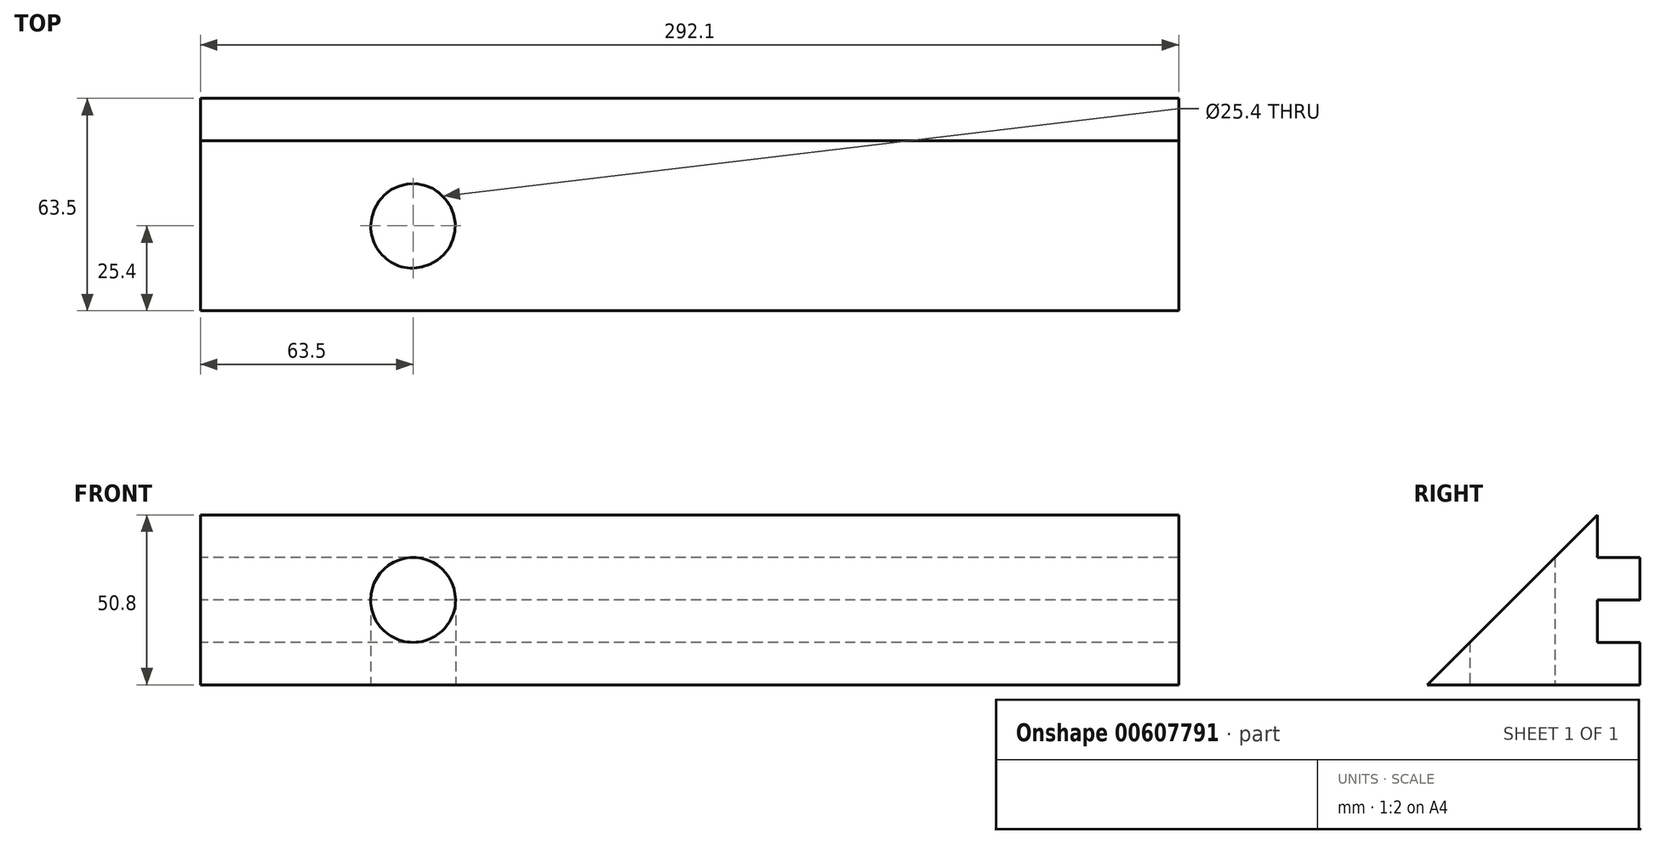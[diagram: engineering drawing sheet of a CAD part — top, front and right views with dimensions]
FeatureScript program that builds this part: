
annotation { "Feature Type Name" : "Feature", "Feature Type Description" : "" }
export const myFeature = defineFeature(function(context is Context, id is Id, definition is map)
    precondition{}
    {
        {
            var Q0;
            Q0=qCreatedBy(makeId("Top.planeOp"),FACE);
            var sketch = newSketch(context, id + "F0", { "sketchPlane" : qUnion([Q0])});
            skLineSegment(sketch, "E0.bottom", {"start": v(0, 0) * mm, "end": v(292.1, 0) * mm});
            skLineSegment(sketch, "E0.top", {"start": v(0, 50.8) * mm, "end": v(292.1, 50.8) * mm});
            skLineSegment(sketch, "E0.left", {"start": v(0, 0) * mm, "end": v(0, 50.8) * mm});
            skLineSegment(sketch, "E0.right", {"start": v(292.1, 0) * mm, "end": v(292.1, 50.8) * mm});
            skLineSegment(sketch, "E1.bottom", {"start": v(0, 0) * mm, "end": v(50.8, 0) * mm});
            skLineSegment(sketch, "E1.top", {"start": v(0, -228.6) * mm, "end": v(50.8, -228.6) * mm});
            skLineSegment(sketch, "E1.left", {"start": v(0, 0) * mm, "end": v(0, -228.6) * mm});
            skLineSegment(sketch, "E1.right", {"start": v(50.8, 0) * mm, "end": v(50.8, -228.6) * mm});
            skLineSegment(sketch, "E2.bottom", {"start": v(292.1, 0) * mm, "end": v(241.3, 0) * mm});
            skLineSegment(sketch, "E2.top", {"start": v(292.1, -228.6) * mm, "end": v(241.3, -228.6) * mm});
            skLineSegment(sketch, "E2.left", {"start": v(292.1, 0) * mm, "end": v(292.1, -228.6) * mm});
            skLineSegment(sketch, "E2.right", {"start": v(241.3, 0) * mm, "end": v(241.3, -228.6) * mm});
            skSolve(sketch);
        }
        {
            var Q0;
            Q0=makeQuery(id+"F0.imprint","IMPRINT",FACE,{"disambiguationData":[TD([[makeQuery(id+"F0.imprint","IMPRINT",EDGE,{"derivedFrom":sQuery(id+"F0.wireOp",EDGE,"E1.bottom")}),-1.0]])]});
            var Q1;
            Q1=makeQuery(id+"F0.imprint","IMPRINT",FACE,{"disambiguationData":[TD([[makeQuery(id+"F0.imprint","IMPRINT",EDGE,{"derivedFrom":sQuery(id+"F0.wireOp",EDGE,"E0.bottom")}),1.0]])]});
            var Q2;
            Q2=makeQuery(id+"F0.imprint","IMPRINT",FACE,{"disambiguationData":[TD([[makeQuery(id+"F0.imprint","IMPRINT",EDGE,{"derivedFrom":sQuery(id+"F0.wireOp",EDGE,"E2.bottom")}),1.0]])]});
            extrude(context, id + "F1", {"entities" : qUnion([Q0, Q1, Q2]), "depth" : 50.8 * mm, "offsetDistance" : 25.4 * mm});
        }
        {
            var Q0;
            Q0=makeQuery(id+"F1.opExtrude","CAP_EDGE",EDGE,{"disambiguationData":[OSD([sQuery(id+"F0.wireOp",EDGE,"E1.right")])],"isStart":false});
            var Q1;
            Q1=makeQuery(id+"F1.opExtrude","CAP_EDGE",EDGE,{"disambiguationData":[OSD([sQuery(id+"F0.wireOp",EDGE,"E0.bottom")])],"isStart":false});
            var Q2;
            Q2=makeQuery(id+"F1.opExtrude","CAP_EDGE",EDGE,{"disambiguationData":[OSD([sQuery(id+"F0.wireOp",EDGE,"E2.right")])],"isStart":false});
            chamfer(context, id + "F2", {"entities" : qUnion([Q0, Q1, Q2]), "width" : 50.8 * mm, "tangentPropagation" : true});
        }
        {
            var Q0;
            Q0=makeQuery(id+"F1.opExtrude","SWEPT_FACE",FACE,{"disambiguationData":[OSD([sQuery(id+"F0.wireOp",EDGE,"E0.top")])]});
            var sketch = newSketch(context, id + "F3", { "sketchPlane" : qUnion([Q0])});
            skLineSegment(sketch, "E3.bottom", {"start": v(-292.1, 50.8) * mm, "end": v(0, 50.8) * mm});
            skLineSegment(sketch, "E3.top", {"start": v(-292.1, 38.1) * mm, "end": v(0, 38.1) * mm});
            skLineSegment(sketch, "E3.left", {"start": v(-292.1, 50.8) * mm, "end": v(-292.1, 38.1) * mm});
            skLineSegment(sketch, "E3.right", {"start": v(0, 50.8) * mm, "end": v(0, 38.1) * mm});
            skLineSegment(sketch, "E4", {"start": v(-292.1, 38.1) * mm, "end": v(-292.1, 25.4) * mm});
            skLineSegment(sketch, "E5.bottom", {"start": v(-292.1, 25.4) * mm, "end": v(0, 25.4) * mm});
            skLineSegment(sketch, "E5.top", {"start": v(-292.1, 12.7) * mm, "end": v(0, 12.7) * mm});
            skLineSegment(sketch, "E5.left", {"start": v(-292.1, 25.4) * mm, "end": v(-292.1, 12.7) * mm});
            skLineSegment(sketch, "E5.right", {"start": v(0, 25.4) * mm, "end": v(0, 12.7) * mm});
            skLineSegment(sketch, "E6", {"start": v(-292.1, 12.7) * mm, "end": v(-292.1, 0) * mm});
            skLineSegment(sketch, "E7.bottom", {"start": v(-292.1, 0) * mm, "end": v(0, 0) * mm});
            skLineSegment(sketch, "E7.top", {"start": v(-292.1, 0) * mm, "end": v(0, 0) * mm});
            skLineSegment(sketch, "E7.left", {"start": v(-292.1, 0) * mm, "end": v(-292.1, 0) * mm});
            skLineSegment(sketch, "E7.right", {"start": v(0, 0) * mm, "end": v(0, 0) * mm});
            skSolve(sketch);
        }
        {
            var Q0;
            Q0=makeQuery(id+"Fjhq9vDB7scd9nn_1.boolean.opBoolean","MERGE",FACE,{"derivedFrom":[makeQuery(id+"F1.opExtrude","CAP_FACE",FACE,{"disambiguationData":[OSD([sQuery(id+"F0.wireOp",EDGE,"E0.bottom"),sQuery(id+"F0.wireOp",EDGE,"E0.top"),sQuery(id+"F0.wireOp",EDGE,"E0.left"),sQuery(id+"F0.wireOp",EDGE,"E0.right"),sQuery(id+"F0.wireOp",EDGE,"E1.top"),sQuery(id+"F0.wireOp",EDGE,"E1.left"),sQuery(id+"F0.wireOp",EDGE,"E1.right"),sQuery(id+"F0.wireOp",EDGE,"E2.top"),sQuery(id+"F0.wireOp",EDGE,"E2.left"),sQuery(id+"F0.wireOp",EDGE,"E2.right")])],"isStart":true}),makeQuery(id+"Fjhq9vDB7scd9nn_1.opExtrude","SWEPT_FACE",FACE,{"disambiguationData":[OSD([sQuery(id+"F3.wireOp",EDGE,"E7.top")])]})]});
            var sketch = newSketch(context, id + "F4", { "sketchPlane" : qUnion([Q0])});
            skCircle(sketch, "E8", {"center": v(63.5, -25.4) * mm, "radius": 12.7 * mm});
            skSolve(sketch);
        }
        {
            var Q0;
            Q0=makeQuery(id+"F4.imprint","IMPRINT",FACE,{"disambiguationData":[TD([[makeQuery(id+"F4.imprint","IMPRINT",EDGE,{"derivedFrom":sQuery(id+"F4.wireOp",EDGE,"E8")}),1.0]])]});
            extrude(context, id + "F5", {"entities" : qUnion([Q0]), "operationType" : NewBodyOperationType.REMOVE, "oppositeDirection" : true, "depth" : 63.5 * mm, "offsetDistance" : 25.4 * mm});
        }
        {
            var Q0;
            {var subQ0=sQuery(id+"F3.wireOp",EDGE,"E5.top");Q0=makeQuery(id+"F3.imprint","IMPRINT",FACE,{"disambiguationData":[TD([[makeQuery(id+"F3.imprint","IMPRINT",EDGE,{"derivedFrom":subQ0}),-1.0]])]});}
            var Q1;
            {var subQ0=sQuery(id+"F3.wireOp",EDGE,"E3.top");Q1=makeQuery(id+"F3.imprint","IMPRINT",FACE,{"disambiguationData":[TD([[makeQuery(id+"F3.imprint","IMPRINT",EDGE,{"derivedFrom":subQ0}),-1.0]])]});}
            extrude(context, id + "F6", {"entities" : qUnion([Q0, Q1]), "operationType" : NewBodyOperationType.ADD, "depth" : 12.7 * mm, "offsetDistance" : 25.4 * mm});
        }
    });
